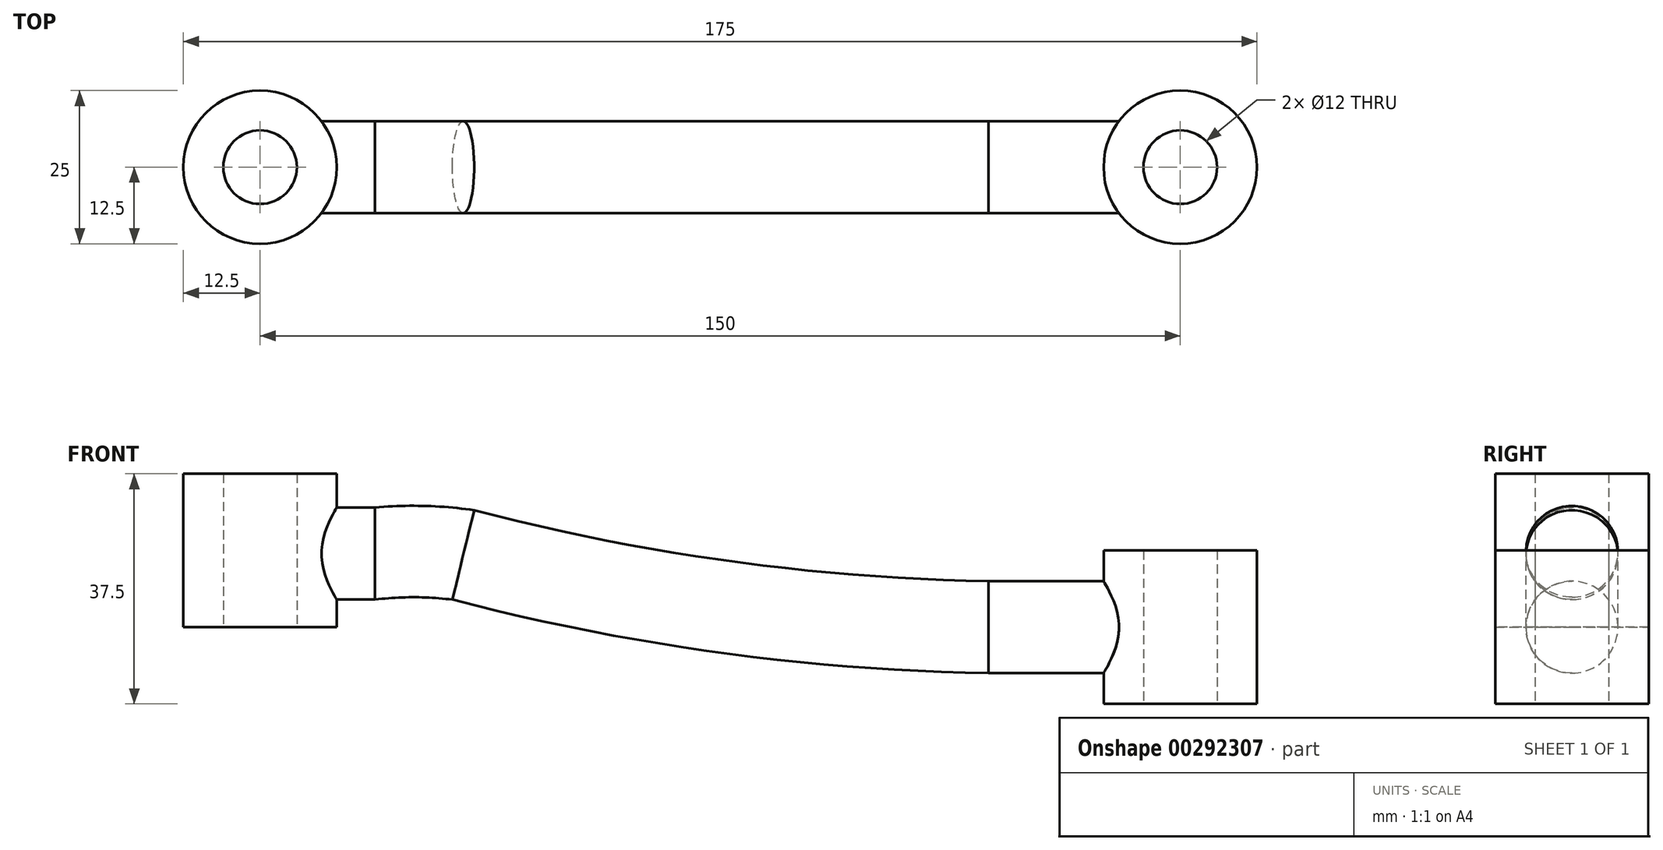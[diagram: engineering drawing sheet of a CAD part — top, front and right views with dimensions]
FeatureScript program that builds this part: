
annotation { "Feature Type Name" : "Feature", "Feature Type Description" : "" }
export const myFeature = defineFeature(function(context is Context, id is Id, definition is map)
    precondition{}
    {
        {
            var Q0;
            Q0=qCreatedBy(makeId("Top.planeOp"),FACE);
            var sketch = newSketch(context, id + "F0", { "sketchPlane" : qUnion([Q0])});
            skCircle(sketch, "E0", {"center": v(-75, 0) * mm, "radius": 12.5 * mm});
            skCircle(sketch, "E1", {"center": v(75, 0) * mm, "radius": 12.5 * mm});
            skLineSegment(sketch, "E2", {"start": v(-75, 0) * mm, "end": v(75, 0) * mm, "construction": true});
            skCircle(sketch, "E3", {"center": v(-75, 0) * mm, "radius": 6 * mm});
            skCircle(sketch, "E4", {"center": v(75, 0) * mm, "radius": 6 * mm});
            skSolve(sketch);
        }
        {
            var Q0;
            Q0=makeQuery(id+"F0.imprint","IMPRINT",FACE,{"disambiguationData":[TD([[makeQuery(id+"F0.imprint","IMPRINT",EDGE,{"derivedFrom":sQuery(id+"F0.wireOp",EDGE,"E0")}),1.0]])]});
            extrude(context, id + "F1", {"entities" : qUnion([Q0]), "depth" : 25 * mm});
        }
        {
            var Q0;
            Q0=makeQuery(id+"F0.imprint","IMPRINT",FACE,{"disambiguationData":[TD([[makeQuery(id+"F0.imprint","IMPRINT",EDGE,{"derivedFrom":sQuery(id+"F0.wireOp",EDGE,"E1")}),1.0]])]});
            extrude(context, id + "F2", {"entities" : qUnion([Q0]), "endBound" : BoundingType.SYMMETRIC, "depth" : 25 * mm});
        }
        {
            var Q0;
            Q0=qCreatedBy(makeId("Front.planeOp"),FACE);
            var sketch = newSketch(context, id + "F3", { "sketchPlane" : qUnion([Q0])});
            skLineSegment(sketch, "E5", {"start": v(-75, 12) * mm, "end": v(-62.5, 12) * mm, "construction": true});
            skArc(sketch, "E6", {"start": v(-50, 12) * mm, "mid": v(-42.85, 11.57) * mm, "end": v(-35.8, 10.3) * mm});
            skArc(sketch, "E7", {"start": v(-35.8, 10.3) * mm, "mid": v(6.79, 2.58) * mm, "end": v(50, 0) * mm});
            skLineSegment(sketch, "E8", {"start": v(62.5, 0) * mm, "end": v(75, 0) * mm, "construction": true});
            skPoint(sketch, "E9", {"position": v(62.5, 0) * mm});
            skLineSegment(sketch, "E10", {"start": v(50, 0) * mm, "end": v(62.5, 0) * mm});
            skPoint(sketch, "E11", {"position": v(-62.5, 12) * mm});
            skLineSegment(sketch, "E12", {"start": v(-62.5, 12) * mm, "end": v(-50, 12) * mm});
            skSolve(sketch);
        }
        {
            var Q0;
            Q0=sQuery(id+"F3.wireOp",EDGE,"E5");
            cPlane(context, id + "F4", {"entities" : qUnion([Q0]), "cplaneType" : CPlaneType.MID_PLANE, "offset" : 25 * mm, "oppositeDirection" : true, "width" : 150 * mm, "height" : 150 * mm});
        }
        {
            var Q0;
            Q0=qCreatedBy(id+"F4.planeOp",FACE);
            var sketch = newSketch(context, id + "F5", { "sketchPlane" : qUnion([Q0])});
            skCircle(sketch, "E13", {"center": v(0, 12) * mm, "radius": 7.5 * mm});
            skSolve(sketch);
        }
        {
            var Q0;
            Q0 = qSketchRegion(id + "F5", true);
            var Q1;
            Q1=sQuery(id+"F3.wireOp",EDGE,"E12");
            var Q2;
            Q2=sQuery(id+"F3.wireOp",EDGE,"E6");
            var Q3;
            Q3=sQuery(id+"F3.wireOp",EDGE,"E7");
            var Q4;
            Q4=sQuery(id+"F3.wireOp",EDGE,"E10");
            sweep(context, id + "F6", {"operationType" : NewBodyOperationType.ADD, "profiles" : qUnion([Q0]), "path" : qUnion([Q1, Q2, Q3, Q4])});
        }
        {
            var Q0;
            Q0=makeQuery(id+"F6.opSweep","CAP_FACE",FACE,{"disambiguationData":[OSD([sQuery(id+"F3.wireOp",VERTEX,"E10.end"),sQuery(id+"F5.wireOp",EDGE,"E13")])],"isStart":false});
            extrude(context, id + "F7", {"entities" : qUnion([Q0]), "operationType" : NewBodyOperationType.ADD, "depth" : 12.5 * mm});
        }
    });
